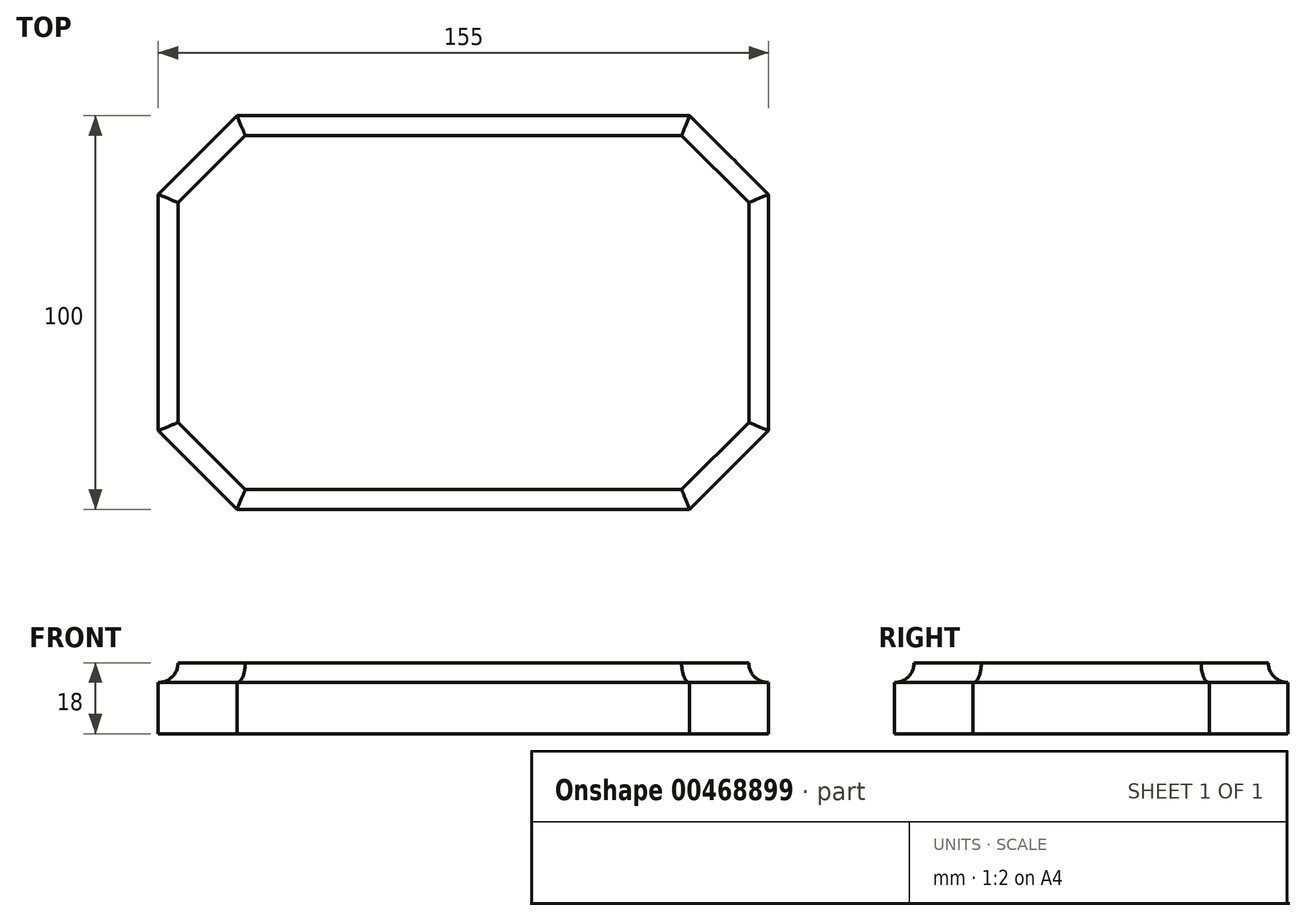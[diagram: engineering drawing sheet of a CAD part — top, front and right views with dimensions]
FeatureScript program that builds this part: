
annotation { "Feature Type Name" : "Feature", "Feature Type Description" : "" }
export const myFeature = defineFeature(function(context is Context, id is Id, definition is map)
    precondition{}
    {
        {
            var Q0;
            Q0=qCreatedBy(makeId("Top.planeOp"),FACE);
            var sketch = newSketch(context, id + "F0", { "sketchPlane" : qUnion([Q0])});
            skLineSegment(sketch, "E0.bottom", {"start": v(0, 0) * mm, "end": v(155, 0) * mm});
            skLineSegment(sketch, "E0.top", {"start": v(0, 100) * mm, "end": v(155, 100) * mm});
            skLineSegment(sketch, "E0.left", {"start": v(0, 0) * mm, "end": v(0, 100) * mm});
            skLineSegment(sketch, "E0.right", {"start": v(155, 0) * mm, "end": v(155, 100) * mm});
            skSolve(sketch);
        }
        {
            var Q0;
            Q0=makeQuery(id+"F0.imprint","IMPRINT",FACE,{"disambiguationData":[TD([[makeQuery(id+"F0.imprint","IMPRINT",EDGE,{"derivedFrom":sQuery(id+"F0.wireOp",EDGE,"E0.bottom")}),1.0]])]});
            extrude(context, id + "F1", {"entities" : qUnion([Q0]), "depth" : 18 * mm});
        }
        {
            var Q0;
            Q0=makeQuery(id+"F1.opExtrude","SWEPT_EDGE",EDGE,{"disambiguationData":[OSD([sQuery(id+"F0.wireOp",EDGE,"E0.top"),sQuery(id+"F0.wireOp",EDGE,"E0.right")])]});
            var Q1;
            Q1=makeQuery(id+"F1.opExtrude","SWEPT_EDGE",EDGE,{"disambiguationData":[OSD([sQuery(id+"F0.wireOp",EDGE,"E0.bottom"),sQuery(id+"F0.wireOp",EDGE,"E0.right")])]});
            var Q2;
            Q2=makeQuery(id+"F1.opExtrude","SWEPT_EDGE",EDGE,{"disambiguationData":[OSD([sQuery(id+"F0.wireOp",EDGE,"E0.top"),sQuery(id+"F0.wireOp",EDGE,"E0.left")])]});
            var Q3;
            Q3=makeQuery(id+"F1.opExtrude","SWEPT_EDGE",EDGE,{"disambiguationData":[OSD([sQuery(id+"F0.wireOp",EDGE,"E0.bottom"),sQuery(id+"F0.wireOp",EDGE,"E0.left")])]});
            chamfer(context, id + "F2", {"entities" : qUnion([Q0, Q1, Q2, Q3]), "width" : 20 * mm, "tangentPropagation" : true});
        }
        {
            var Q0;
            Q0=qCreatedBy(makeId("Front.planeOp"),FACE);
            cPlane(context, id + "F3", {"entities" : qUnion([Q0]), "cplaneType" : CPlaneType.OFFSET, "offset" : 25 * mm, "oppositeDirection" : true, "width" : 150 * mm, "height" : 150 * mm});
        }
        {
            var Q0;
            Q0=qCreatedBy(id+"F3.planeOp",FACE);
            var sketch = newSketch(context, id + "F4", { "sketchPlane" : qUnion([Q0])});
            skPoint(sketch, "E1.0", {"position": v(0, 18) * mm});
            skCircle(sketch, "E2", {"center": v(0, 18) * mm, "radius": 5 * mm});
            skSolve(sketch);
        }
        {
            var Q0;
            Q0=makeQuery(id+"F1.opExtrude","CAP_FACE",FACE,{"disambiguationData":[OSD([sQuery(id+"F0.wireOp",EDGE,"E0.bottom"),sQuery(id+"F0.wireOp",EDGE,"E0.top"),sQuery(id+"F0.wireOp",EDGE,"E0.left"),sQuery(id+"F0.wireOp",EDGE,"E0.right")])],"isStart":false});
            var sketch = newSketch(context, id + "F5", { "sketchPlane" : qUnion([Q0])});
            skLineSegment(sketch, "E3", {"start": v(0, 25) * mm, "end": v(0, 80) * mm});
            skLineSegment(sketch, "E4", {"start": v(0, 80) * mm, "end": v(20, 100) * mm});
            skLineSegment(sketch, "E5", {"start": v(20, 100) * mm, "end": v(135.02, 100) * mm});
            skLineSegment(sketch, "E6", {"start": v(135.02, 100) * mm, "end": v(155, 80) * mm});
            skLineSegment(sketch, "E7", {"start": v(155, 80) * mm, "end": v(155, 20) * mm});
            skLineSegment(sketch, "E8", {"start": v(155, 20) * mm, "end": v(135, 0) * mm});
            skLineSegment(sketch, "E9", {"start": v(135, 0) * mm, "end": v(20, 0) * mm});
            skLineSegment(sketch, "E10", {"start": v(20, 0) * mm, "end": v(0, 20) * mm});
            skLineSegment(sketch, "E11", {"start": v(0, 20) * mm, "end": v(0, 25) * mm});
            skSolve(sketch);
        }
        {
            var Q0;
            Q0=makeQuery(id+"F4.imprint","IMPRINT",FACE,{"disambiguationData":[TD([[makeQuery(id+"F4.imprint","IMPRINT",EDGE,{"derivedFrom":sQuery(id+"F4.wireOp",EDGE,"E2")}),1.0]])]});
            var Q1;
            Q1=sQuery(id+"F4.wireOp",EDGE,"E2");
            var Q2;
            Q2=sQuery(id+"F5.wireOp",EDGE,"E4");
            var Q3;
            Q3=sQuery(id+"F5.wireOp",EDGE,"E5");
            var Q4;
            Q4=sQuery(id+"F5.wireOp",EDGE,"E6");
            var Q5;
            Q5=sQuery(id+"F5.wireOp",EDGE,"E7");
            var Q6;
            Q6=sQuery(id+"F5.wireOp",EDGE,"E8");
            var Q7;
            Q7=sQuery(id+"F5.wireOp",EDGE,"E9");
            var Q8;
            Q8=sQuery(id+"F5.wireOp",EDGE,"E10");
            var Q9;
            Q9=sQuery(id+"F5.wireOp",EDGE,"E11");
            var Q10;
            Q10=sQuery(id+"F5.wireOp",EDGE,"E3");
            sweep(context, id + "F6", {"operationType" : NewBodyOperationType.REMOVE, "profiles" : qUnion([Q0]), "surfaceProfiles" : qUnion([Q1]), "path" : qUnion([Q2, Q3, Q4, Q5, Q6, Q7, Q8, Q9, Q10])});
        }
    });
